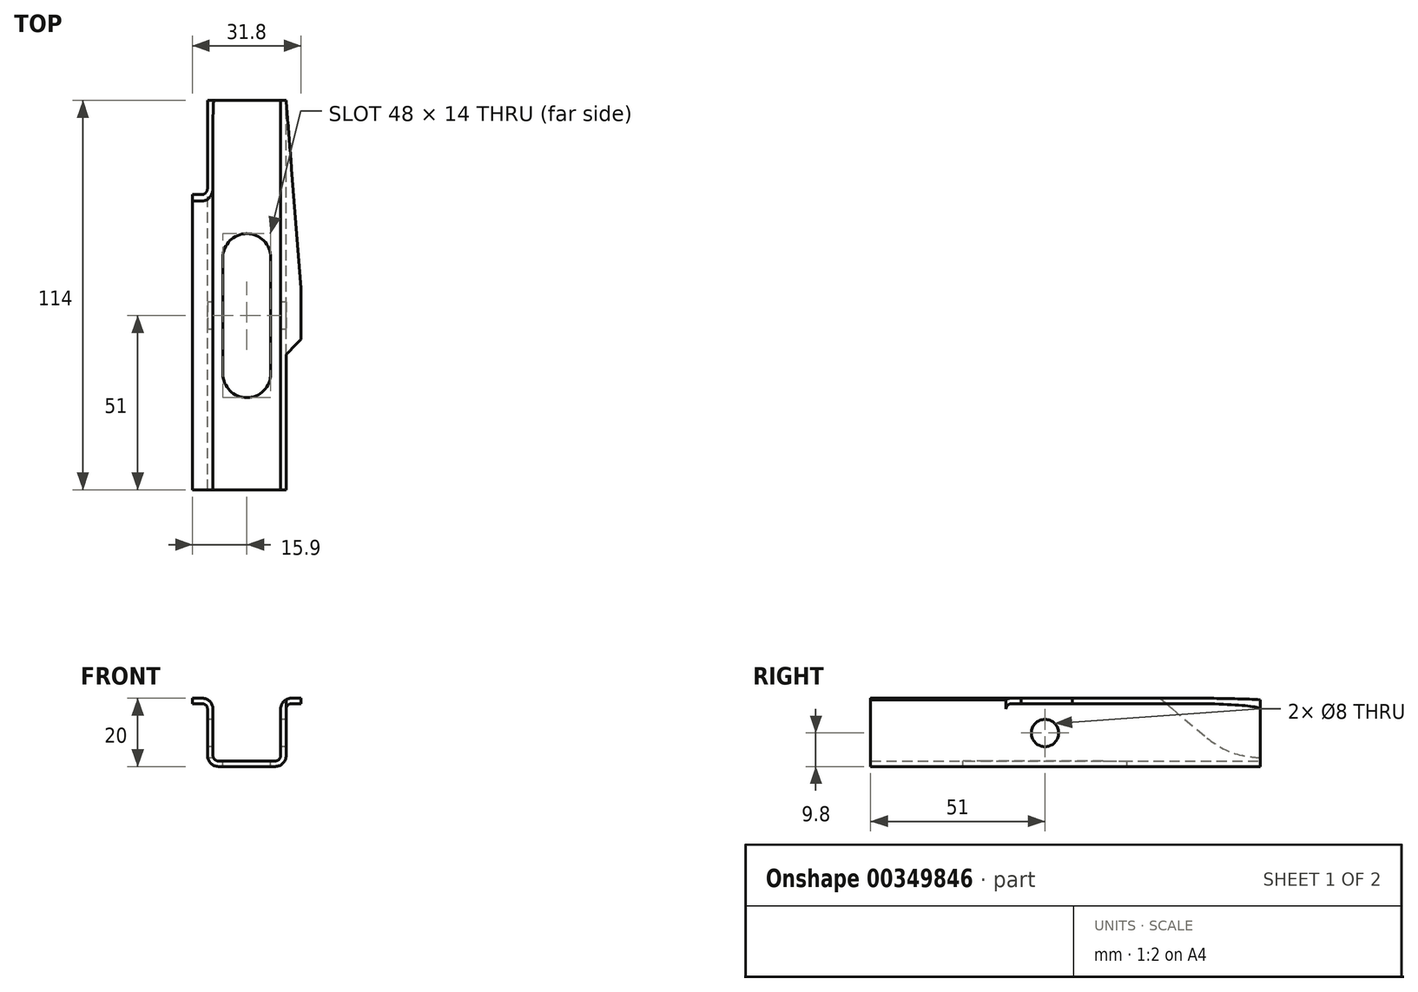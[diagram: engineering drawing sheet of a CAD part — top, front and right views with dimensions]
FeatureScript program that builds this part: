
annotation { "Feature Type Name" : "Feature", "Feature Type Description" : "" }
export const myFeature = defineFeature(function(context is Context, id is Id, definition is map)
    precondition{}
    {
        {
            var Q0;
            Q0=qCreatedBy(makeId("Front.planeOp"),FACE);
            var sketch = newSketch(context, id + "F0", { "sketchPlane" : qUnion([Q0])});
            skLineSegment(sketch, "E0", {"start": v(-8.3, 0) * mm, "end": v(0, 0) * mm});
            skLineSegment(sketch, "E1", {"start": v(-8.3, 1.6) * mm, "end": v(0, 1.6) * mm});
            skLineSegment(sketch, "E2", {"start": v(-11.5, 3.2) * mm, "end": v(-11.5, 16.8) * mm});
            skLineSegment(sketch, "E3", {"start": v(-9.9, 3.2) * mm, "end": v(-9.9, 16.8) * mm});
            skLineSegment(sketch, "E4", {"start": v(-13.1, 20) * mm, "end": v(-15.9, 20) * mm});
            skLineSegment(sketch, "E5", {"start": v(-15.9, 20) * mm, "end": v(-15.9, 18.4) * mm});
            skPoint(sketch, "E6.endSnap0", {"position": v(-15.9, 18.08) * mm});
            skPoint(sketch, "E7.orphan", {"position": v(-26.3, 18.08) * mm});
            skPoint(sketch, "E8.orphan", {"position": v(-15.9, 16.17) * mm});
            skLineSegment(sketch, "E9", {"start": v(-13.1, 18.4) * mm, "end": v(-15.9, 18.4) * mm});
            skPoint(sketch, "E10.visualSharp", {"position": v(-11.5, 18.4) * mm});
            skArc(sketch, "E10.filletArc", {"start": v(-11.5, 16.8) * mm, "mid": v(-11.97, 17.93) * mm, "end": v(-13.1, 18.4) * mm});
            skPoint(sketch, "E11.visualSharp", {"position": v(-9.9, 1.6) * mm});
            skArc(sketch, "E11.filletArc", {"start": v(-9.9, 3.2) * mm, "mid": v(-9.43, 2.07) * mm, "end": v(-8.3, 1.6) * mm});
            skPoint(sketch, "E12.visualSharp", {"position": v(-9.9, 20) * mm});
            skArc(sketch, "E12.filletArc", {"start": v(-9.9, 16.8) * mm, "mid": v(-10.84, 19.06) * mm, "end": v(-13.1, 20) * mm});
            skPoint(sketch, "E13.visualSharp", {"position": v(-11.5, 0) * mm});
            skArc(sketch, "E13.filletArc", {"start": v(-11.5, 3.2) * mm, "mid": v(-10.56, 0.94) * mm, "end": v(-8.3, 0) * mm});
            skLineSegment(sketch, "E14", {"start": v(0, 0) * mm, "end": v(0, 25.46) * mm, "construction": true});
            skLineSegment(sketch, "E15.MirrorCS", {"start": v(15.9, 20) * mm, "end": v(15.9, 18.4) * mm});
            skPoint(sketch, "E16.MirrorP", {"position": v(26.3, 18.08) * mm});
            skArc(sketch, "E17.MirrorCS", {"start": v(9.9, 3.2) * mm, "mid": v(9.43, 2.07) * mm, "end": v(8.3, 1.6) * mm});
            skArc(sketch, "E18.MirrorCS", {"start": v(11.5, 16.8) * mm, "mid": v(11.97, 17.93) * mm, "end": v(13.1, 18.4) * mm});
            skLineSegment(sketch, "E19.MirrorCS", {"start": v(8.3, 0) * mm, "end": v(0, 0) * mm});
            skLineSegment(sketch, "E20.MirrorCS", {"start": v(8.3, 1.6) * mm, "end": v(0, 1.6) * mm});
            skPoint(sketch, "E21.MirrorP", {"position": v(9.9, 1.6) * mm});
            skLineSegment(sketch, "E22.MirrorCS", {"start": v(11.5, 3.2) * mm, "end": v(11.5, 16.8) * mm});
            skLineSegment(sketch, "E23.MirrorCS", {"start": v(9.9, 3.2) * mm, "end": v(9.9, 16.8) * mm});
            skPoint(sketch, "E24.MirrorP", {"position": v(15.9, 18.08) * mm});
            skPoint(sketch, "E25.MirrorP", {"position": v(15.9, 16.17) * mm});
            skPoint(sketch, "E26.MirrorP", {"position": v(11.5, 18.4) * mm});
            skArc(sketch, "E27.MirrorCS", {"start": v(11.5, 3.2) * mm, "mid": v(10.56, 0.94) * mm, "end": v(8.3, 0) * mm});
            skLineSegment(sketch, "E28.MirrorCS", {"start": v(13.1, 18.4) * mm, "end": v(15.9, 18.4) * mm});
            skArc(sketch, "E29.MirrorCS", {"start": v(9.9, 16.8) * mm, "mid": v(10.84, 19.06) * mm, "end": v(13.1, 20) * mm});
            skPoint(sketch, "E30.MirrorP", {"position": v(9.9, 20) * mm});
            skPoint(sketch, "E31.MirrorP", {"position": v(11.5, 0) * mm});
            skLineSegment(sketch, "E32.MirrorCS", {"start": v(13.1, 20) * mm, "end": v(15.9, 20) * mm});
            skSolve(sketch);
        }
        {
            var Q0;
            Q0=qSketchRegion(id+"F0",true);
            extrude(context, id + "F1", {"entities" : qUnion([Q0]), "depth" : 114 * mm});
        }
        {
            var Q0;
            Q0=makeQuery(id+"F1.opExtrude","SWEPT_FACE",FACE,{"disambiguationData":[OSD([sQuery(id+"F0.wireOp",EDGE,"E1"),sQuery(id+"F0.wireOp",EDGE,"E20.MirrorCS")])]});
            var sketch = newSketch(context, id + "F2", { "sketchPlane" : qUnion([Q0])});
            skLineSegment(sketch, "E33.bottom", {"start": v(7, -46) * mm, "end": v(-7, -46) * mm});
            skLineSegment(sketch, "E33.top", {"start": v(7, -80) * mm, "end": v(-7, -80) * mm});
            skLineSegment(sketch, "E33.left", {"start": v(7, -46) * mm, "end": v(7, -80) * mm});
            skLineSegment(sketch, "E33.right", {"start": v(-7, -46) * mm, "end": v(-7, -80) * mm});
            skPoint(sketch, "E33.middle", {"position": v(0, -63) * mm});
            skLineSegment(sketch, "E34", {"start": v(0, 0) * mm, "end": v(0, -144.93) * mm, "construction": true});
            skCircle(sketch, "E35", {"center": v(0, -46) * mm, "radius": 7 * mm});
            skCircle(sketch, "E36", {"center": v(0, -80) * mm, "radius": 7 * mm});
            skSolve(sketch);
        }
        {
            var Q0;
            Q0=qSketchRegion(id+"F2",true);
            extrude(context, id + "F3", {"entities" : qUnion([Q0]), "operationType" : NewBodyOperationType.REMOVE, "oppositeDirection" : true, "depth" : 25 * mm});
        }
        {
            var Q0;
            Q0=makeQuery(id+"F1.opExtrude","SWEPT_FACE",FACE,{"disambiguationData":[OSD([sQuery(id+"F0.wireOp",EDGE,"E4")])]});
            var sketch = newSketch(context, id + "F4", { "sketchPlane" : qUnion([Q0])});
            skLineSegment(sketch, "E37", {"start": v(-15.9, 0) * mm, "end": v(-11.5, 0) * mm});
            skPoint(sketch, "E37.endSnap0", {"position": v(-14.5, 0) * mm});
            skLineSegment(sketch, "E38", {"start": v(-11.5, 0) * mm, "end": v(-15.9, -55) * mm});
            skLineSegment(sketch, "E39", {"start": v(-15.9, -55) * mm, "end": v(-15.9, 0) * mm});
            skLineSegment(sketch, "E40", {"start": v(-15.9, -70) * mm, "end": v(-11.5, -74.4) * mm});
            skLineSegment(sketch, "E41", {"start": v(-11.5, -74.4) * mm, "end": v(-11.5, -114) * mm});
            skLineSegment(sketch, "E42", {"start": v(-11.5, -114) * mm, "end": v(-15.9, -114) * mm});
            skLineSegment(sketch, "E43", {"start": v(-15.9, -114) * mm, "end": v(-15.9, -70) * mm});
            skSolve(sketch);
        }
        {
            var Q0;
            Q0=qSketchRegion(id+"F4",true);
            extrude(context, id + "F5", {"entities" : qUnion([Q0]), "operationType" : NewBodyOperationType.REMOVE, "oppositeDirection" : true, "depth" : 5 * mm});
        }
        {
            var Q0;
            Q0=makeQuery(id+"F1.opExtrude","SWEPT_FACE",FACE,{"disambiguationData":[OSD([sQuery(id+"F0.wireOp",EDGE,"E22.MirrorCS")])]});
            var sketch = newSketch(context, id + "F6", { "sketchPlane" : qUnion([Q0])});
            skCircle(sketch, "E44", {"center": v(-63, 9.8) * mm, "radius": 4 * mm});
            skSolve(sketch);
        }
        {
            var Q0;
            Q0=qSketchRegion(id+"F6",true);
            extrude(context, id + "F7", {"entities" : qUnion([Q0]), "operationType" : NewBodyOperationType.REMOVE, "oppositeDirection" : true, "depth" : 30 * mm});
        }
        {
            var Q0;
            Q0=makeQuery(id+"F1.opExtrude","SWEPT_FACE",FACE,{"disambiguationData":[OSD([sQuery(id+"F0.wireOp",EDGE,"E22.MirrorCS")])]});
            var sketch = newSketch(context, id + "F8", { "sketchPlane" : qUnion([Q0])});
            skArc(sketch, "E45", {"start": v(-15.57, 8.35) * mm, "mid": v(-8.05, 4) * mm, "end": v(0.5, 2.5) * mm});
            skLineSegment(sketch, "E46", {"start": v(-15.57, 8.35) * mm, "end": v(-38.4, 27.5) * mm});
            skLineSegment(sketch, "E47", {"start": v(0.5, 2.5) * mm, "end": v(5, 2.5) * mm});
            skLineSegment(sketch, "E48", {"start": v(5, 2.5) * mm, "end": v(5, 27.5) * mm});
            skLineSegment(sketch, "E49", {"start": v(-38.4, 27.5) * mm, "end": v(5, 27.5) * mm});
            skSolve(sketch);
        }
        {
            var Q0;
            Q0=qSketchRegion(id+"F8",true);
            extrude(context, id + "F9", {"entities" : qUnion([Q0]), "operationType" : NewBodyOperationType.REMOVE, "endBound" : BoundingType.SYMMETRIC, "oppositeDirection" : true, "depth" : 10 * mm});
        }
        {
            var Q0;
            Q0=makeQuery(id+"F1.opExtrude","SWEPT_BODY",BODY,{"disambiguationData":[OSD([sQuery(id+"F0.wireOp",EDGE,"E0"),sQuery(id+"F0.wireOp",EDGE,"E1"),sQuery(id+"F0.wireOp",EDGE,"E2"),sQuery(id+"F0.wireOp",EDGE,"E3"),sQuery(id+"F0.wireOp",EDGE,"E4"),sQuery(id+"F0.wireOp",EDGE,"E5"),sQuery(id+"F0.wireOp",EDGE,"E9"),sQuery(id+"F0.wireOp",EDGE,"E10.filletArc"),sQuery(id+"F0.wireOp",EDGE,"E11.filletArc"),sQuery(id+"F0.wireOp",EDGE,"E12.filletArc"),sQuery(id+"F0.wireOp",EDGE,"E13.filletArc"),sQuery(id+"F0.wireOp",EDGE,"E15.MirrorCS"),sQuery(id+"F0.wireOp",EDGE,"E17.MirrorCS"),sQuery(id+"F0.wireOp",EDGE,"E18.MirrorCS"),sQuery(id+"F0.wireOp",EDGE,"E19.MirrorCS"),sQuery(id+"F0.wireOp",EDGE,"E20.MirrorCS"),sQuery(id+"F0.wireOp",EDGE,"E22.MirrorCS"),sQuery(id+"F0.wireOp",EDGE,"E23.MirrorCS"),sQuery(id+"F0.wireOp",EDGE,"E27.MirrorCS"),sQuery(id+"F0.wireOp",EDGE,"E28.MirrorCS"),sQuery(id+"F0.wireOp",EDGE,"E29.MirrorCS"),sQuery(id+"F0.wireOp",EDGE,"E32.MirrorCS")])]});
            var Q1;
            {var subQ0=sQuery(id+"F0.wireOp",EDGE,"E22.MirrorCS");var subQ1=makeQuery(id+"F1.opExtrude","CAP_EDGE",EDGE,{"disambiguationData":[OSD([subQ0])],"isStart":false});Q1=makeQuery(id+"F8.imprint","IMPRINT",FACE,{"disambiguationData":[TD([[makeQuery(id+"F8.imprint","IMPRINT",EDGE,{"derivedFrom":subQ1}),-1.0]])]});}
            mirror(context, id + "F10", {"entities" : qUnion([Q0]), "mirrorPlane" : qUnion([Q1])});
        }
        {
            var Q0;
            Q0=makeQuery(id+"F1.opExtrude","SWEPT_BODY",BODY,{"disambiguationData":[OSD([sQuery(id+"F0.wireOp",EDGE,"E0"),sQuery(id+"F0.wireOp",EDGE,"E1"),sQuery(id+"F0.wireOp",EDGE,"E2"),sQuery(id+"F0.wireOp",EDGE,"E3"),sQuery(id+"F0.wireOp",EDGE,"E4"),sQuery(id+"F0.wireOp",EDGE,"E5"),sQuery(id+"F0.wireOp",EDGE,"E9"),sQuery(id+"F0.wireOp",EDGE,"E10.filletArc"),sQuery(id+"F0.wireOp",EDGE,"E11.filletArc"),sQuery(id+"F0.wireOp",EDGE,"E12.filletArc"),sQuery(id+"F0.wireOp",EDGE,"E13.filletArc"),sQuery(id+"F0.wireOp",EDGE,"E15.MirrorCS"),sQuery(id+"F0.wireOp",EDGE,"E17.MirrorCS"),sQuery(id+"F0.wireOp",EDGE,"E18.MirrorCS"),sQuery(id+"F0.wireOp",EDGE,"E19.MirrorCS"),sQuery(id+"F0.wireOp",EDGE,"E20.MirrorCS"),sQuery(id+"F0.wireOp",EDGE,"E22.MirrorCS"),sQuery(id+"F0.wireOp",EDGE,"E23.MirrorCS"),sQuery(id+"F0.wireOp",EDGE,"E27.MirrorCS"),sQuery(id+"F0.wireOp",EDGE,"E28.MirrorCS"),sQuery(id+"F0.wireOp",EDGE,"E29.MirrorCS"),sQuery(id+"F0.wireOp",EDGE,"E32.MirrorCS")])]});
            deleteBodies(context, id + "F11", {"entities" : qUnion([Q0])});
        }
    });
